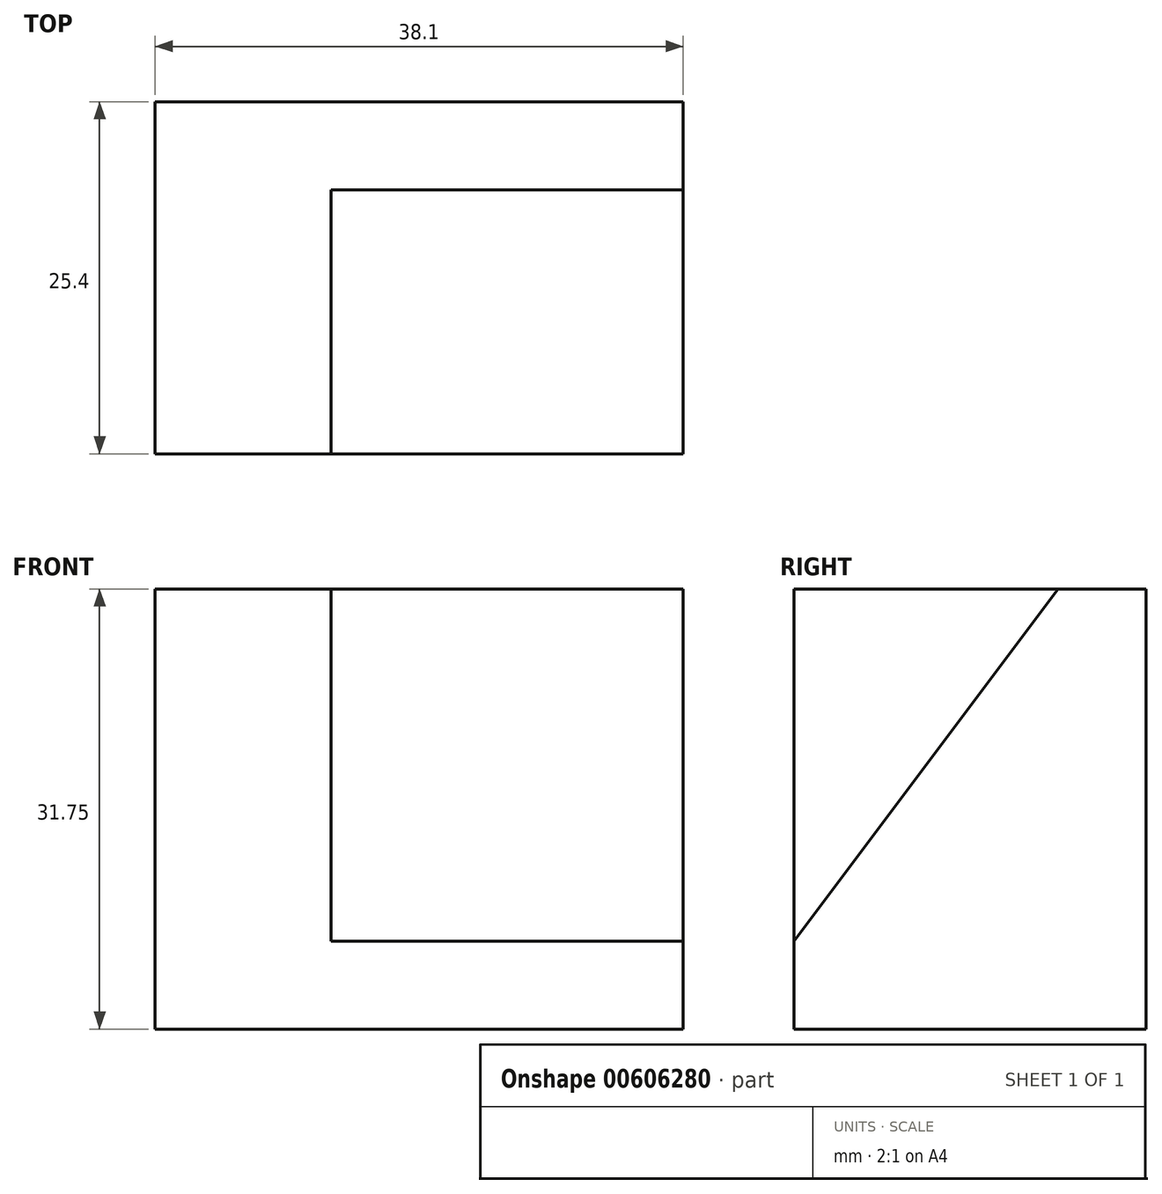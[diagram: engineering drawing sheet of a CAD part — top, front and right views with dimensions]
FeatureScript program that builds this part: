
annotation { "Feature Type Name" : "Feature", "Feature Type Description" : "" }
export const myFeature = defineFeature(function(context is Context, id is Id, definition is map)
    precondition{}
    {
        {
            var Q0;
            Q0=qCreatedBy(makeId("Right.planeOp"),FACE);
            var sketch = newSketch(context, id + "F0", { "sketchPlane" : qUnion([Q0])});
            skLineSegment(sketch, "E0", {"start": v(0, 0) * mm, "end": v(25.4, 0) * mm});
            skLineSegment(sketch, "E1", {"start": v(0, 0) * mm, "end": v(0, 31.75) * mm});
            skLineSegment(sketch, "E2", {"start": v(0, 31.75) * mm, "end": v(19.05, 31.75) * mm});
            skLineSegment(sketch, "E3", {"start": v(19.05, 31.75) * mm, "end": v(25.4, 31.75) * mm});
            skLineSegment(sketch, "E4", {"start": v(25.4, 31.75) * mm, "end": v(25.4, 0) * mm});
            skLineSegment(sketch, "E5", {"start": v(0, 0) * mm, "end": v(0, 6.35) * mm});
            skLineSegment(sketch, "E6", {"start": v(0, 6.35) * mm, "end": v(19.05, 31.75) * mm});
            skSolve(sketch);
        }
        {
            var Q0;
            Q0=makeQuery(id+"F0.imprint","IMPRINT",FACE,{"disambiguationData":[TD([[makeQuery(id+"F0.imprint","IMPRINT",EDGE,{"derivedFrom":sQuery(id+"F0.wireOp",EDGE,"E0")}),1.0]])]});
            extrude(context, id + "F1", {"entities" : qUnion([Q0]), "depth" : 38.1 * mm, "offsetDistance" : 25.4 * mm});
        }
        {
            var Q0;
            Q0=makeQuery(id+"F0.imprint","IMPRINT",FACE,{"disambiguationData":[TD([[makeQuery(id+"F0.imprint","IMPRINT",EDGE,{"derivedFrom":sQuery(id+"F0.wireOp",EDGE,"E1")}),-1.0]])]});
            extrude(context, id + "F2", {"entities" : qUnion([Q0]), "operationType" : NewBodyOperationType.ADD, "depth" : 12.7 * mm, "offsetDistance" : 25.4 * mm});
        }
    });
